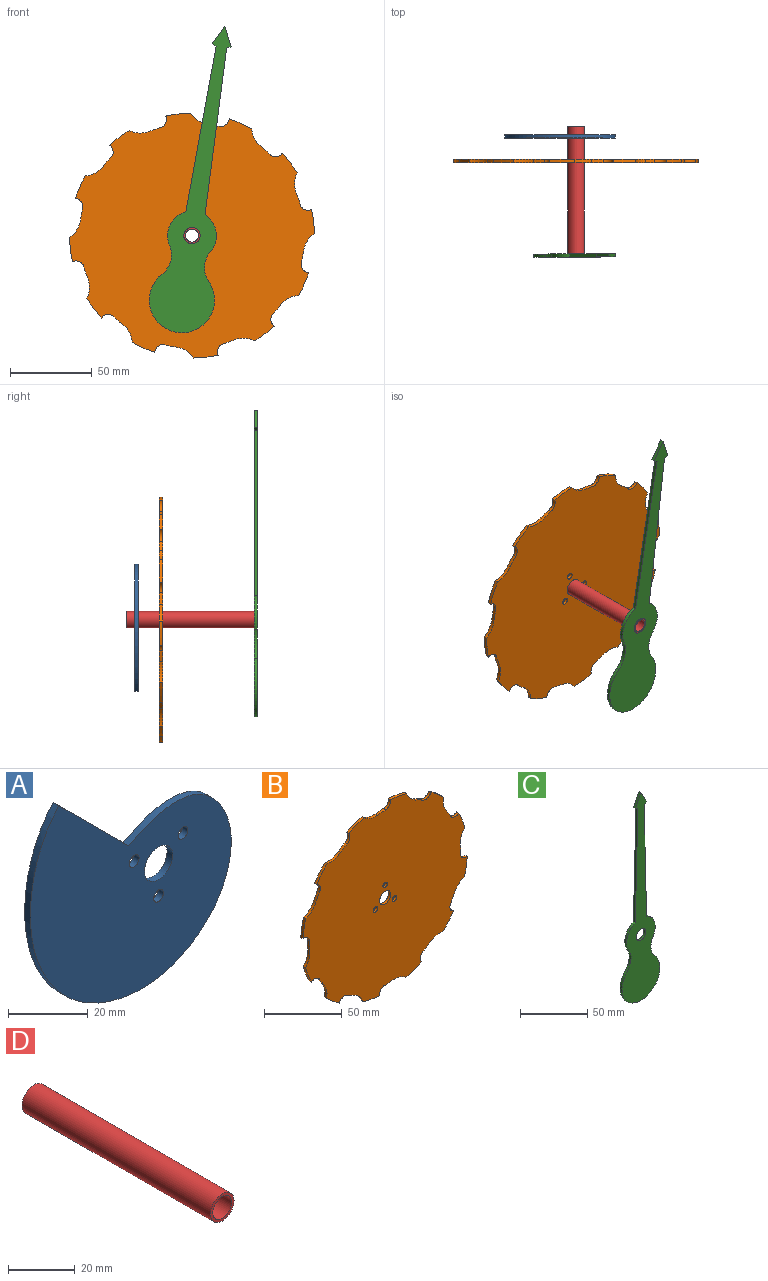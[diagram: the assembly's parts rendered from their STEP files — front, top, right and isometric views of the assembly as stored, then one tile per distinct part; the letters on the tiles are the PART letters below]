
ASSEMBLY  parts=4 mates=5
PART A: 8 faces, bbox 72.9x2x71.7 mm
  f0: extruded ~71.13x70.76mm, area 387.9mm2, adj f1,f3,f4
  f1: plane 24.75x24.75mm, normal (0.71,0,0.71), area 70mm2, adj f0,f3,f4
  f2: cylinder r=5mm len=10mm, axis (0,1,0), area 62.8mm2, adj f3,f4
  f3: plane 72.86x71.69mm, normal (0,-1,0), area 3161.4mm2, adj f0,f1,f2,f5,f6,f7
  f4: plane 72.86x71.69mm, normal (0,1,0), area 3161.4mm2, adj f0,f1,f2,f5,f6,f7
  f5: cylinder r=1.75mm len=3.5mm, axis (0,-1,0), area 22mm2, adj f3,f4
  f6: cylinder r=1.75mm len=3.5mm, axis (0,-1,0), area 22mm2, adj f3,f4
  f7: cylinder r=1.75mm len=3.5mm, axis (0,-1,0), area 22mm2, adj f3,f4
PART B: 54 faces, bbox 149.7x2x149.7 mm
  f0: cylinder r=75mm len=11.65mm, axis (0,1,0), area 30.3mm2, adj f13,f14,f47,f48
  f1: cylinder r=75mm len=14.9mm, axis (0,1,0), area 30.3mm2, adj f13,f14,f44,f45
  f2: cylinder r=75mm len=14.16mm, axis (0,1,0), area 30.3mm2, adj f13,f14,f41,f42
  f3: cylinder r=75mm len=11.65mm, axis (0,1,0), area 30.3mm2, adj f13,f14,f38,f39
  f4: cylinder r=75mm len=14.9mm, axis (0,1,0), area 30.3mm2, adj f13,f14,f35,f36
  f5: cylinder r=75mm len=14.16mm, axis (0,1,0), area 30.3mm2, adj f13,f14,f32,f33
  f6: cylinder r=75mm len=11.65mm, axis (0,1,0), area 30.3mm2, adj f13,f14,f29,f30
  f7: cylinder r=75mm len=14.9mm, axis (0,1,0), area 30.3mm2, adj f13,f14,f17,f27
  f8: cylinder r=75mm len=14.16mm, axis (0,1,0), area 30.3mm2, adj f13,f14,f24,f50
  f9: cylinder r=75mm len=14.9mm, axis (0,1,0), area 30.3mm2, adj f13,f14,f21,f26
  f10: cylinder r=75mm len=11.65mm, axis (0,1,0), area 30.3mm2, adj f13,f14,f18,f23
  f11: cylinder r=5mm len=10mm, axis (0,1,0), area 62.8mm2, adj f13,f14
  f12: cylinder r=75mm len=14.16mm, axis (0,1,0), area 30.3mm2, adj f13,f14,f15,f20
  f13: plane 149.68x149.68mm, normal (0,-1,0), area 16158.8mm2, adj f0,f1,f2,f3,f4,f5,f6,f7
  f14: plane 149.68x149.68mm, normal (0,1,0), area 16158.8mm2, adj f0,f1,f2,f3,f4,f5,f6,f7
  f15: cylinder r=15mm len=11.78mm, axis (0,-1,0), area 25.6mm2, adj f12,f13,f14,f16
  f16: cylinder r=69mm len=7.21mm, axis (0,-1,0), area 14.5mm2, adj f13,f14,f15,f17
  f17: cylinder r=5mm len=5.84mm, axis (0,-1,0), area 17.4mm2, adj f7,f13,f14,f16
  f18: cylinder r=15mm len=12.17mm, axis (0,-1,0), area 25.6mm2, adj f10,f13,f14,f19
  f19: cylinder r=69mm len=6.06mm, axis (0,-1,0), area 14.5mm2, adj f13,f14,f18,f20
  f20: cylinder r=5mm len=7.52mm, axis (0,-1,0), area 17.4mm2, adj f12,f13,f14,f19
  f21: cylinder r=15mm len=9.3mm, axis (0,-1,0), area 25.6mm2, adj f9,f13,f14,f22
  f22: cylinder r=69mm len=6.44mm, axis (0,-1,0), area 14.5mm2, adj f13,f14,f21,f23
  f23: cylinder r=5mm len=7.19mm, axis (0,-1,0), area 17.4mm2, adj f10,f13,f14,f22
  f24: cylinder r=15mm len=11.78mm, axis (0,-1,0), area 25.6mm2, adj f8,f13,f14,f25
  f25: cylinder r=69mm len=7.21mm, axis (0,-1,0), area 14.5mm2, adj f13,f14,f24,f26
  f26: cylinder r=5mm len=5.84mm, axis (0,-1,0), area 17.4mm2, adj f9,f13,f14,f25
  f27: cylinder r=15mm len=9.3mm, axis (0,-1,0), area 25.6mm2, adj f7,f13,f14,f28
  f28: cylinder r=69mm len=6.44mm, axis (0,-1,0), area 14.5mm2, adj f13,f14,f27,f29
  f29: cylinder r=5mm len=7.19mm, axis (0,-1,0), area 17.4mm2, adj f6,f13,f14,f28
  f30: cylinder r=15mm len=12.17mm, axis (0,-1,0), area 25.6mm2, adj f6,f13,f14,f31
  f31: cylinder r=69mm len=6.06mm, axis (0,-1,0), area 14.5mm2, adj f13,f14,f30,f32
  f32: cylinder r=5mm len=7.52mm, axis (0,-1,0), area 17.4mm2, adj f5,f13,f14,f31
  f33: cylinder r=15mm len=11.78mm, axis (0,-1,0), area 25.6mm2, adj f5,f13,f14,f34
  f34: cylinder r=69mm len=7.21mm, axis (0,-1,0), area 14.5mm2, adj f13,f14,f33,f35
  f35: cylinder r=5mm len=5.84mm, axis (0,-1,0), area 17.4mm2, adj f4,f13,f14,f34
  f36: cylinder r=15mm len=9.3mm, axis (0,-1,0), area 25.6mm2, adj f4,f13,f14,f37
  f37: cylinder r=69mm len=6.44mm, axis (0,-1,0), area 14.5mm2, adj f13,f14,f36,f38
  f38: cylinder r=5mm len=7.19mm, axis (0,-1,0), area 17.4mm2, adj f3,f13,f14,f37
  f39: cylinder r=15mm len=12.17mm, axis (0,-1,0), area 25.6mm2, adj f3,f13,f14,f40
  f40: cylinder r=69mm len=6.06mm, axis (0,-1,0), area 14.5mm2, adj f13,f14,f39,f41
  f41: cylinder r=5mm len=7.52mm, axis (0,-1,0), area 17.4mm2, adj f2,f13,f14,f40
  f42: cylinder r=15mm len=11.78mm, axis (0,-1,0), area 25.6mm2, adj f2,f13,f14,f43
  f43: cylinder r=69mm len=7.21mm, axis (0,-1,0), area 14.5mm2, adj f13,f14,f42,f44
  f44: cylinder r=5mm len=5.84mm, axis (0,-1,0), area 17.4mm2, adj f1,f13,f14,f43
  f45: cylinder r=15mm len=9.3mm, axis (0,-1,0), area 25.6mm2, adj f1,f13,f14,f46
  f46: cylinder r=69mm len=6.44mm, axis (0,-1,0), area 14.5mm2, adj f13,f14,f45,f47
  f47: cylinder r=5mm len=7.19mm, axis (0,-1,0), area 17.4mm2, adj f0,f13,f14,f46
  f48: cylinder r=15mm len=12.17mm, axis (0,-1,0), area 25.6mm2, adj f0,f13,f14,f49
  f49: cylinder r=69mm len=6.06mm, axis (0,-1,0), area 14.5mm2, adj f13,f14,f48,f50
  f50: cylinder r=5mm len=7.52mm, axis (0,-1,0), area 17.4mm2, adj f8,f13,f14,f49
  f51: cylinder r=2mm len=4mm, axis (0,-1,0), area 25.1mm2, adj f13,f14
  f52: cylinder r=2mm len=4mm, axis (0,-1,0), area 25.1mm2, adj f13,f14
  f53: cylinder r=2mm len=4mm, axis (0,-1,0), area 25.1mm2, adj f13,f14
PART C: 14 faces, bbox 40x2x190 mm
  f0: plane 2.69x2mm, normal (0.45,0,-0.89), area 6mm2, adj f1,f10,f12,f13
  f1: plane 11.91x5.95mm, normal (0.89,0,0.45), area 26.6mm2, adj f0,f2,f12,f13
  f2: plane 11.91x5.95mm, normal (-0.89,0,0.45), area 26.6mm2, adj f1,f3,f12,f13
  f3: plane 2.69x2mm, normal (-0.45,0,-0.89), area 6mm2, adj f2,f4,f12,f13
  f4: plane 102.98x2.69mm, normal (-1,0,0.03), area 206mm2, adj f3,f5,f12,f13
  f5: cylinder r=15mm len=21.74mm, axis (0,1,0), area 51.7mm2, adj f4,f6,f12,f13
  f6: cylinder r=15mm len=18.28mm, axis (0,1,0), area 39.5mm2, adj f5,f7,f12,f13
  f7: cylinder r=20mm len=40mm, axis (0,1,0), area 186.3mm2, adj f6,f8,f12,f13
  f8: cylinder r=15mm len=18.28mm, axis (0,1,0), area 39.5mm2, adj f7,f9,f12,f13
  f9: cylinder r=15mm len=21.74mm, axis (0,1,0), area 51.7mm2, adj f8,f10,f12,f13
  f10: plane 102.98x2.69mm, normal (1,0,0.03), area 206mm2, adj f0,f9,f12,f13
  f11: cylinder r=5mm len=10mm, axis (0,1,0), area 62.8mm2, adj f12,f13
  f12: plane 190x40mm, normal (0,-1,0), area 3073.4mm2, adj f0,f1,f2,f3,f4,f5,f6,f7
  f13: plane 190x40mm, normal (0,1,0), area 3073.4mm2, adj f0,f1,f2,f3,f4,f5,f6,f7
PART D: 4 faces, bbox 10x80x10 mm
  f0: cylinder r=4mm len=80mm, axis (0,1,0), area 2010.6mm2, adj f2,f3
  f1: cylinder r=5mm len=80mm, axis (0,1,0), area 2513.3mm2, adj f2,f3
  f2: plane 10x10mm, normal (0,-1,0), area 28.3mm2, adj f0,f1
  f3: plane 10x10mm, normal (0,1,0), area 28.3mm2, adj f0,f1
PLACE A rot(axis=(0.99,0,0.14),180deg) t=(165.83,31.41,18.03)mm
PLACE B rot(axis=(0,-1,0),16.1deg) t=(165.83,18.41,18.03)mm
PLACE C rot(axis=(0,1,0),8.9deg) t=(165.83,-39.59,18.03)mm
PLACE D t=(165.83,38.41,18.03)mm
MATE slider B.f52 <-> A.f6  axis (0,1,0) through (175.54,18.41,15.63)mm
MATE revolute D.f1 <-> A.f2  axis (0,1,0) through (165.83,38.41,18.03)mm
MATE revolute D.f1 <-> B.f11  axis (0,1,0) through (165.83,38.41,18.03)mm
MATE cylindrical D.f1 <-> C.f11  axis (0,1,0) through (165.83,-1.59,18.03)mm
MATE planar D.f1 <-> C.f12  axis (0,-1,0) through (165.83,-41.59,18.03)mm
